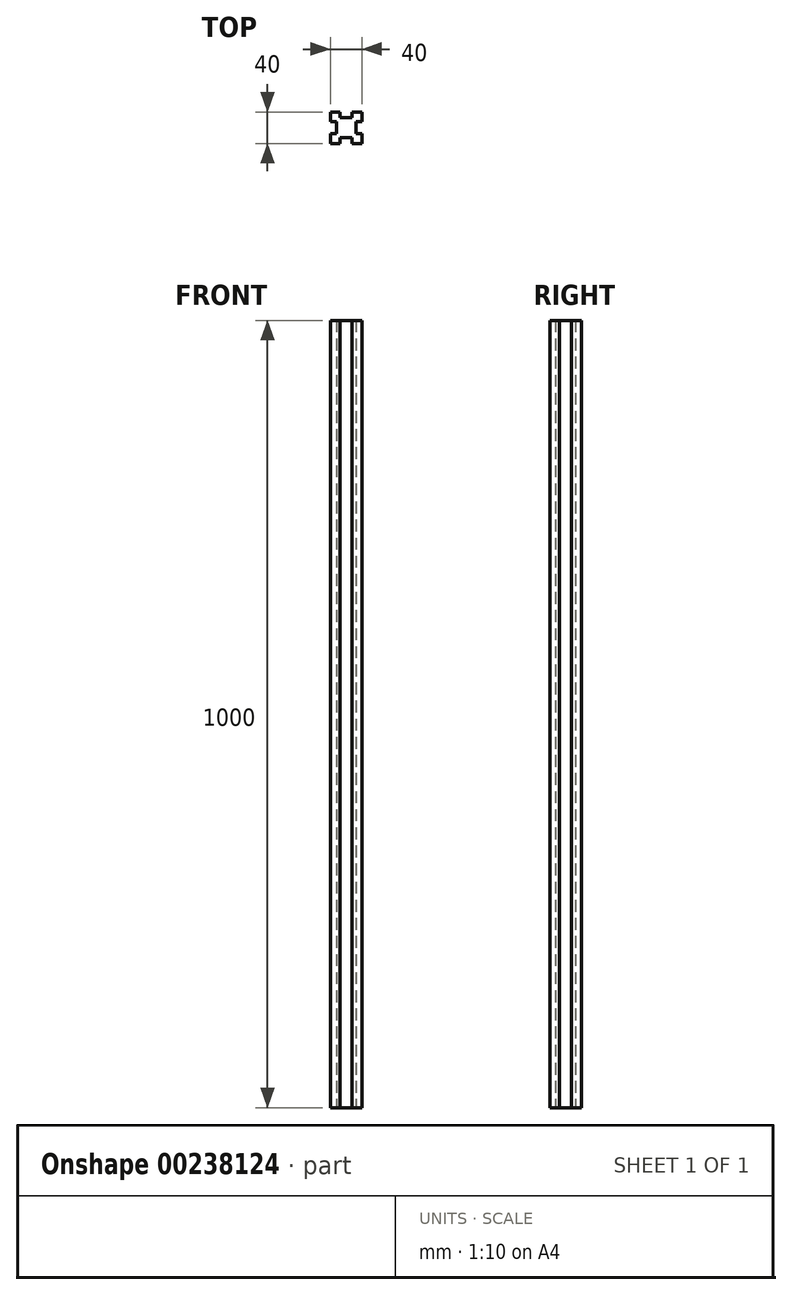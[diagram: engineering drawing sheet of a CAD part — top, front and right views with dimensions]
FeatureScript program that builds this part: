
annotation { "Feature Type Name" : "Feature", "Feature Type Description" : "" }
export const myFeature = defineFeature(function(context is Context, id is Id, definition is map)
    precondition{}
    {
        {
            var Q0;
            Q0=qCreatedBy(makeId("Top.planeOp"),FACE);
            var sketch = newSketch(context, id + "F0", { "sketchPlane" : qUnion([Q0])});
            skLineSegment(sketch, "E0.bottom", {"start": v(20, 20) * mm, "end": v(7.5, 20) * mm});
            skLineSegment(sketch, "E0.top", {"start": v(20, -20) * mm, "end": v(7.5, -20) * mm});
            skLineSegment(sketch, "E0.left", {"start": v(20, 20) * mm, "end": v(20, 7.5) * mm});
            skLineSegment(sketch, "E0.right", {"start": v(-20, 20) * mm, "end": v(-20, 7.5) * mm});
            skPoint(sketch, "E0.middle", {"position": v(0, 0) * mm});
            skLineSegment(sketch, "E1.top", {"start": v(7.5, 12.5) * mm, "end": v(-7.5, 12.5) * mm});
            skLineSegment(sketch, "E1.left", {"start": v(7.5, 20) * mm, "end": v(7.5, 12.5) * mm});
            skLineSegment(sketch, "E1.right", {"start": v(-7.5, 20) * mm, "end": v(-7.5, 12.5) * mm});
            skPoint(sketch, "E1.middle", {"position": v(0, 20) * mm});
            skLineSegment(sketch, "E2.bottom", {"start": v(20, 7.5) * mm, "end": v(12.5, 7.5) * mm});
            skLineSegment(sketch, "E2.top", {"start": v(20, -7.5) * mm, "end": v(12.5, -7.5) * mm});
            skLineSegment(sketch, "E2.right", {"start": v(12.5, 7.5) * mm, "end": v(12.5, -7.5) * mm});
            skPoint(sketch, "E2.middle", {"position": v(20, 0) * mm});
            skLineSegment(sketch, "E3.bottom", {"start": v(7.5, -12.5) * mm, "end": v(-7.5, -12.5) * mm});
            skLineSegment(sketch, "E3.left", {"start": v(7.5, -12.5) * mm, "end": v(7.5, -20) * mm});
            skLineSegment(sketch, "E3.right", {"start": v(-7.5, -12.5) * mm, "end": v(-7.5, -20) * mm});
            skPoint(sketch, "E3.middle", {"position": v(0, -20) * mm});
            skLineSegment(sketch, "E4.bottom", {"start": v(-12.5, 7.5) * mm, "end": v(-20, 7.5) * mm});
            skLineSegment(sketch, "E4.top", {"start": v(-12.5, -7.5) * mm, "end": v(-20, -7.5) * mm});
            skLineSegment(sketch, "E4.left", {"start": v(-12.5, 7.5) * mm, "end": v(-12.5, -7.5) * mm});
            skPoint(sketch, "E4.middle", {"position": v(-20, 0) * mm});
            skLineSegment(sketch, "E5.trimOffspring", {"start": v(-7.5, 20) * mm, "end": v(-20, 20) * mm});
            skPoint(sketch, "E1.bottom.end.orphan", {"position": v(-7.5, 27.5) * mm});
            skPoint(sketch, "E6.orphan", {"position": v(7.5, 27.5) * mm});
            skPoint(sketch, "E2.left.start.orphan", {"position": v(27.5, 7.5) * mm});
            skLineSegment(sketch, "E7.trimOffspring", {"start": v(20, -7.5) * mm, "end": v(20, -20) * mm});
            skPoint(sketch, "E8.orphan", {"position": v(27.5, -7.5) * mm});
            skLineSegment(sketch, "E9.trimOffspring", {"start": v(-7.5, -20) * mm, "end": v(-20, -20) * mm});
            skPoint(sketch, "E3.top.end.orphan", {"position": v(-7.5, -27.5) * mm});
            skPoint(sketch, "E3.top.start.orphan", {"position": v(7.5, -27.5) * mm});
            skLineSegment(sketch, "E10.trimOffspring", {"start": v(-20, -7.5) * mm, "end": v(-20, -20) * mm});
            skPoint(sketch, "E11.orphan", {"position": v(-27.5, 7.5) * mm});
            skPoint(sketch, "E12.orphan", {"position": v(-27.5, -7.5) * mm});
            skSolve(sketch);
        }
        {
            var Q0;
            Q0 = qSketchRegion(id + "F0", true);
            extrude(context, id + "F1", {"entities" : qUnion([Q0]), "depth" : 1000 * mm});
        }
    });
